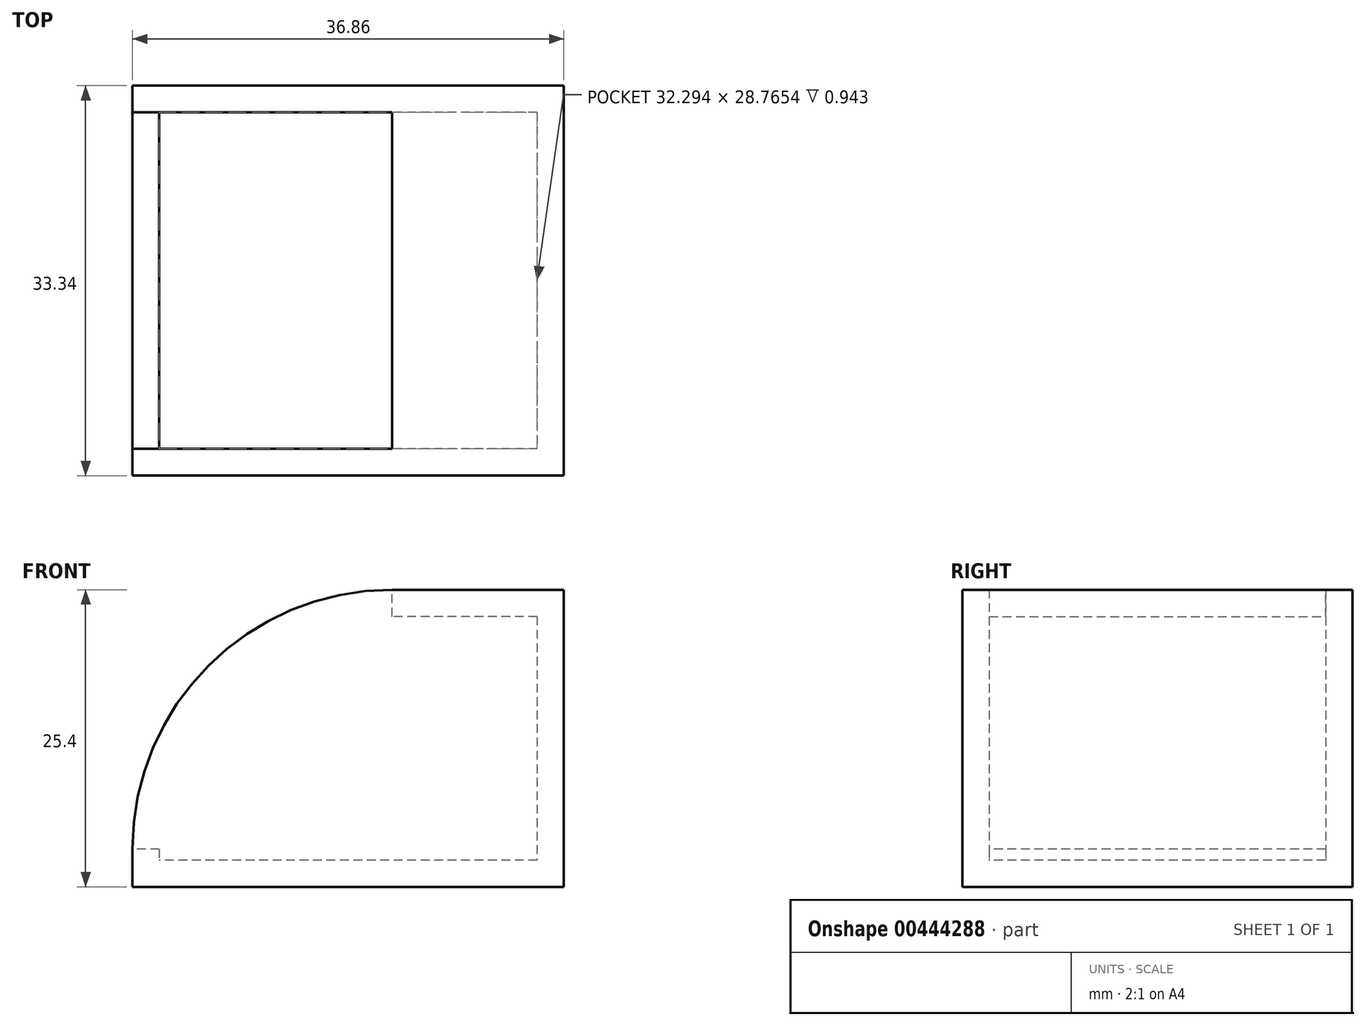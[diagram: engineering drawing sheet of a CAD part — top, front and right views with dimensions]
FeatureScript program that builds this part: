
annotation { "Feature Type Name" : "Feature", "Feature Type Description" : "" }
export const myFeature = defineFeature(function(context is Context, id is Id, definition is map)
    precondition{}
    {
        {
            var Q0;
            Q0=qCreatedBy(makeId("Top.planeOp"),FACE);
            var sketch = newSketch(context, id + "F0", { "sketchPlane" : qUnion([Q0])});
            skLineSegment(sketch, "E0.bottom", {"start": v(18.43, 16.67) * mm, "end": v(-18.43, 16.67) * mm});
            skLineSegment(sketch, "E0.top", {"start": v(18.43, -16.67) * mm, "end": v(-18.43, -16.67) * mm});
            skLineSegment(sketch, "E0.left", {"start": v(18.43, 16.67) * mm, "end": v(18.43, -16.67) * mm});
            skLineSegment(sketch, "E0.right", {"start": v(-18.43, 16.67) * mm, "end": v(-18.43, -16.67) * mm});
            skPoint(sketch, "E0.middle", {"position": v(0, 0) * mm});
            skSolve(sketch);
        }
        {
            var Q0;
            Q0 = qSketchRegion(id + "F0", true);
            extrude(context, id + "F1", {"entities" : qUnion([Q0]), "depth" : 25.4 * mm});
        }
        {
            var Q0;
            Q0=makeQuery(id+"F1.opExtrude","CAP_EDGE",EDGE,{"disambiguationData":[OSD([sQuery(id+"F0.wireOp",EDGE,"E0.right")])],"isStart":false});
            fillet(context, id + "F2", {"entities" : qUnion([Q0]), "radius" : 22.17 * mm, "tangentPropagation" : true, "allowEdgeOverflow" : false});
        }
        {
            var Q0;
            Q0=makeQuery(id+"F2.opFillet","BLEND_FACE",FACE,{"disambiguationData":[OSD([sQuery(id+"F0.wireOp",EDGE,"E0.right")])]});
            shell(context, id + "F3", {"entities" : qUnion([Q0]), "thickness" : 2.3 * mm});
        }
    });
